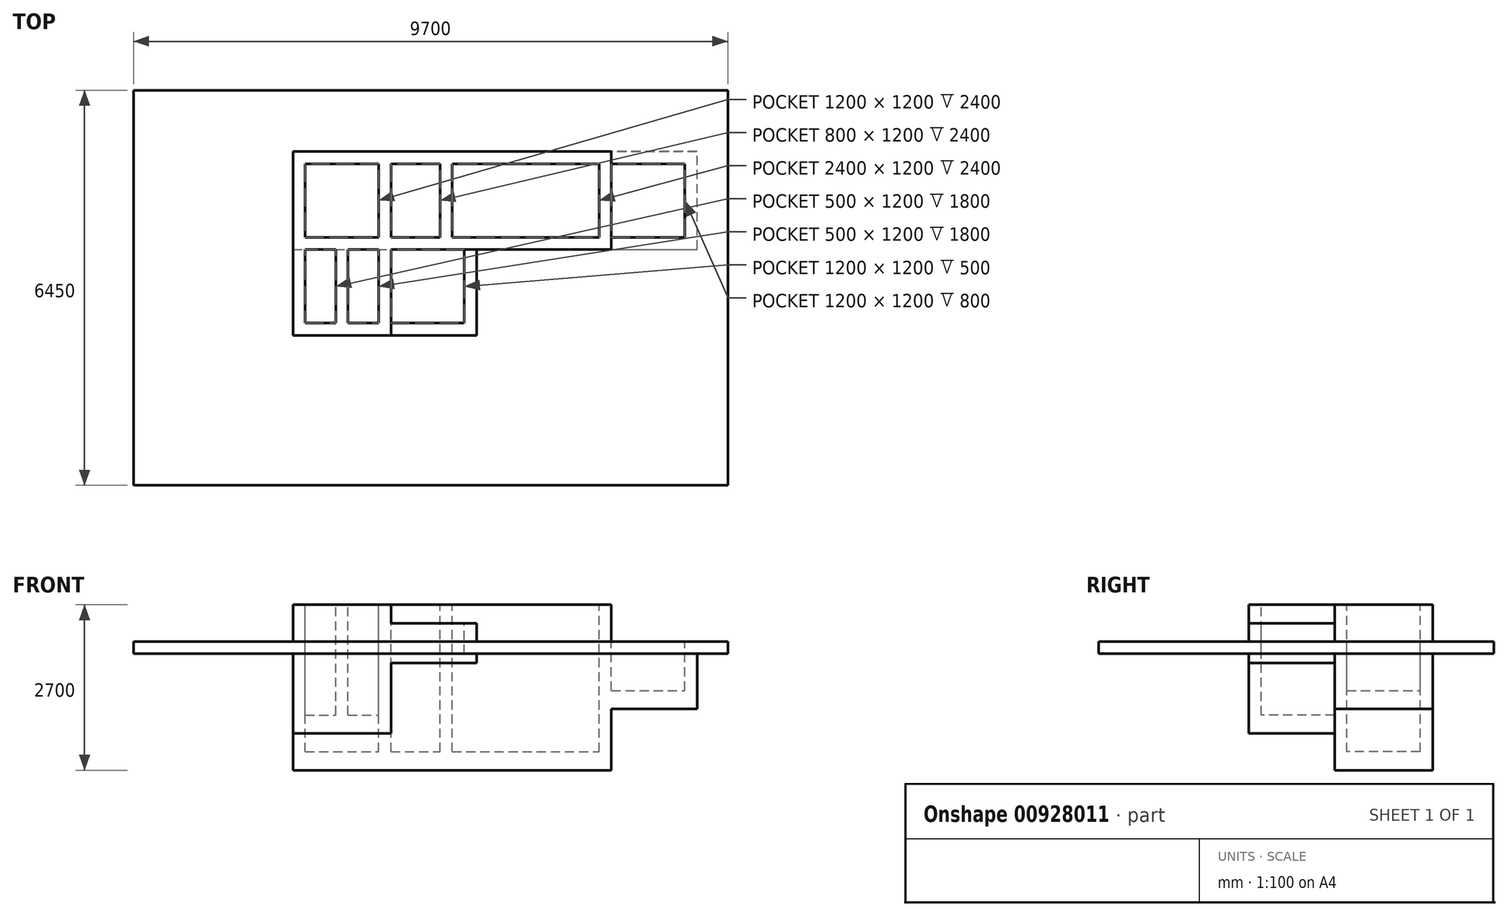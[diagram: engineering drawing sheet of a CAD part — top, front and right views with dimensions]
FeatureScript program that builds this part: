
annotation { "Feature Type Name" : "Feature", "Feature Type Description" : "" }
export const myFeature = defineFeature(function(context is Context, id is Id, definition is map)
    precondition{}
    {
        {
            var Q0;
            Q0=qCreatedBy(makeId("Top.planeOp"),FACE);
            var sketch = newSketch(context, id + "F0", { "sketchPlane" : qUnion([Q0])});
            skLineSegment(sketch, "E0.bottom", {"start": v(0, 0) * mm, "end": v(3000, 0) * mm});
            skLineSegment(sketch, "E0.top", {"start": v(0, 3000) * mm, "end": v(5200, 3000) * mm});
            skLineSegment(sketch, "E0.left", {"start": v(0, 0) * mm, "end": v(0, 3000) * mm});
            skLineSegment(sketch, "E0.right", {"start": v(5200, 1400) * mm, "end": v(5200, 3000) * mm});
            skLineSegment(sketch, "E1", {"start": v(5200, 1400) * mm, "end": v(3000, 1400) * mm});
            skLineSegment(sketch, "E2", {"start": v(3000, 1400) * mm, "end": v(3000, 0) * mm});
            skLineSegment(sketch, "E3.bottom", {"start": v(200, 2800) * mm, "end": v(1400, 2800) * mm});
            skLineSegment(sketch, "E3.top", {"start": v(200, 1600) * mm, "end": v(1400, 1600) * mm});
            skLineSegment(sketch, "E3.left", {"start": v(200, 2800) * mm, "end": v(200, 1600) * mm});
            skLineSegment(sketch, "E3.right", {"start": v(1400, 2800) * mm, "end": v(1400, 1600) * mm});
            skLineSegment(sketch, "E4.bottom", {"start": v(1600, 2800) * mm, "end": v(2400, 2800) * mm});
            skLineSegment(sketch, "E4.top", {"start": v(1600, 1600) * mm, "end": v(2400, 1600) * mm});
            skLineSegment(sketch, "E4.left", {"start": v(1600, 2800) * mm, "end": v(1600, 1600) * mm});
            skLineSegment(sketch, "E4.right", {"start": v(2400, 2800) * mm, "end": v(2400, 1600) * mm});
            skLineSegment(sketch, "E5.bottom", {"start": v(2600, 2800) * mm, "end": v(5000, 2800) * mm});
            skLineSegment(sketch, "E5.top", {"start": v(2600, 1600) * mm, "end": v(5000, 1600) * mm});
            skLineSegment(sketch, "E5.left", {"start": v(2600, 2800) * mm, "end": v(2600, 1600) * mm});
            skLineSegment(sketch, "E5.right", {"start": v(5000, 2800) * mm, "end": v(5000, 1600) * mm});
            skLineSegment(sketch, "E6", {"start": v(5200, 1400) * mm, "end": v(6600, 1400) * mm});
            skLineSegment(sketch, "E7", {"start": v(6600, 1400) * mm, "end": v(6600, 3000) * mm});
            skLineSegment(sketch, "E8", {"start": v(6600, 3000) * mm, "end": v(5200, 3000) * mm});
            skLineSegment(sketch, "E9.bottom", {"start": v(5200, 2800) * mm, "end": v(6400, 2800) * mm});
            skLineSegment(sketch, "E9.top", {"start": v(5200, 1600) * mm, "end": v(6400, 1600) * mm});
            skLineSegment(sketch, "E9.left", {"start": v(5200, 2800) * mm, "end": v(5200, 1600) * mm});
            skLineSegment(sketch, "E9.right", {"start": v(6400, 2800) * mm, "end": v(6400, 1600) * mm});
            skLineSegment(sketch, "E10.bottom", {"start": v(200, 1400) * mm, "end": v(700, 1400) * mm});
            skLineSegment(sketch, "E10.top", {"start": v(200, 200) * mm, "end": v(700, 200) * mm});
            skLineSegment(sketch, "E10.left", {"start": v(200, 1400) * mm, "end": v(200, 200) * mm});
            skLineSegment(sketch, "E10.right", {"start": v(700, 1400) * mm, "end": v(700, 200) * mm});
            skLineSegment(sketch, "E11.bottom", {"start": v(900, 1400) * mm, "end": v(1400, 1400) * mm});
            skLineSegment(sketch, "E11.top", {"start": v(900, 200) * mm, "end": v(1400, 200) * mm});
            skLineSegment(sketch, "E11.left", {"start": v(900, 1400) * mm, "end": v(900, 200) * mm});
            skLineSegment(sketch, "E11.right", {"start": v(1400, 1400) * mm, "end": v(1400, 200) * mm});
            skLineSegment(sketch, "E12.bottom", {"start": v(1600, 1400) * mm, "end": v(2800, 1400) * mm});
            skLineSegment(sketch, "E12.top", {"start": v(1600, 200) * mm, "end": v(2800, 200) * mm});
            skLineSegment(sketch, "E12.left", {"start": v(1600, 1400) * mm, "end": v(1600, 200) * mm});
            skLineSegment(sketch, "E12.right", {"start": v(2800, 1400) * mm, "end": v(2800, 200) * mm});
            skLineSegment(sketch, "E13", {"start": v(1400, 2800) * mm, "end": v(1400, 3000) * mm});
            skLineSegment(sketch, "E14", {"start": v(1400, 1600) * mm, "end": v(1400, 1400) * mm});
            skLineSegment(sketch, "E15", {"start": v(1600, 1400) * mm, "end": v(1600, 1600) * mm});
            skLineSegment(sketch, "E16", {"start": v(1400, 1600) * mm, "end": v(1600, 1600) * mm});
            skLineSegment(sketch, "E17", {"start": v(1600, 1400) * mm, "end": v(1400, 1400) * mm});
            skLineSegment(sketch, "E18", {"start": v(2600, 1600) * mm, "end": v(2600, 1400) * mm});
            skLineSegment(sketch, "E19", {"start": v(2400, 1600) * mm, "end": v(2400, 1400) * mm});
            skLineSegment(sketch, "E20", {"start": v(2600, 1600) * mm, "end": v(2400, 1600) * mm});
            skLineSegment(sketch, "E21", {"start": v(1600, 2800) * mm, "end": v(1600, 3000) * mm});
            skLineSegment(sketch, "E22", {"start": v(2400, 2800) * mm, "end": v(2400, 3000) * mm});
            skLineSegment(sketch, "E23", {"start": v(2600, 2800) * mm, "end": v(2600, 3000) * mm});
            skLineSegment(sketch, "E24", {"start": v(2400, 2800) * mm, "end": v(2600, 2800) * mm});
            skLineSegment(sketch, "E25", {"start": v(1600, 2800) * mm, "end": v(1400, 2800) * mm});
            skLineSegment(sketch, "E26", {"start": v(200, 2800) * mm, "end": v(200, 3000) * mm});
            skLineSegment(sketch, "E27", {"start": v(200, 2800) * mm, "end": v(0, 2800) * mm});
            skLineSegment(sketch, "E28", {"start": v(900, 1400) * mm, "end": v(900, 1600) * mm});
            skLineSegment(sketch, "E29", {"start": v(700, 1400) * mm, "end": v(700, 1600) * mm});
            skLineSegment(sketch, "E30", {"start": v(900, 1400) * mm, "end": v(700, 1400) * mm});
            skLineSegment(sketch, "E31", {"start": v(200, 1400) * mm, "end": v(200, 1600) * mm});
            skLineSegment(sketch, "E32", {"start": v(200, 1400) * mm, "end": v(0, 1400) * mm});
            skLineSegment(sketch, "E33", {"start": v(200, 1600) * mm, "end": v(0, 1600) * mm});
            skLineSegment(sketch, "E34", {"start": v(200, 200) * mm, "end": v(0, 200) * mm});
            skLineSegment(sketch, "E35", {"start": v(700, 200) * mm, "end": v(900, 200) * mm});
            skLineSegment(sketch, "E36", {"start": v(1400, 200) * mm, "end": v(1600, 200) * mm});
            skLineSegment(sketch, "E37", {"start": v(2800, 200) * mm, "end": v(3000, 200) * mm});
            skLineSegment(sketch, "E38", {"start": v(2800, 200) * mm, "end": v(2800, 0) * mm});
            skLineSegment(sketch, "E39", {"start": v(1600, 200) * mm, "end": v(1600, 0) * mm});
            skLineSegment(sketch, "E40", {"start": v(1400, 200) * mm, "end": v(1400, 0) * mm});
            skLineSegment(sketch, "E41", {"start": v(700, 200) * mm, "end": v(700, 0) * mm});
            skLineSegment(sketch, "E42", {"start": v(900, 200) * mm, "end": v(900, 0) * mm});
            skLineSegment(sketch, "E43", {"start": v(200, 200) * mm, "end": v(200, 0) * mm});
            skLineSegment(sketch, "E44", {"start": v(2800, 1400) * mm, "end": v(3000, 1400) * mm});
            skLineSegment(sketch, "E45", {"start": v(5000, 1600) * mm, "end": v(5200, 1600) * mm});
            skLineSegment(sketch, "E46", {"start": v(5200, 2800) * mm, "end": v(5000, 2800) * mm});
            skLineSegment(sketch, "E47", {"start": v(5000, 2800) * mm, "end": v(5000, 3000) * mm});
            skLineSegment(sketch, "E48", {"start": v(5200, 2800) * mm, "end": v(5200, 3000) * mm});
            skLineSegment(sketch, "E49", {"start": v(6400, 2800) * mm, "end": v(6400, 3000) * mm});
            skLineSegment(sketch, "E50", {"start": v(6400, 2800) * mm, "end": v(6600, 2800) * mm});
            skLineSegment(sketch, "E51", {"start": v(6400, 1600) * mm, "end": v(6600, 1600) * mm});
            skLineSegment(sketch, "E52", {"start": v(6400, 1600) * mm, "end": v(6400, 1400) * mm});
            skLineSegment(sketch, "E53", {"start": v(5200, 1600) * mm, "end": v(5200, 1400) * mm});
            skLineSegment(sketch, "E54", {"start": v(5000, 1600) * mm, "end": v(5000, 1400) * mm});
            skPoint(sketch, "E55.orphan", {"position": v(5200, 3000) * mm});
            skSolve(sketch);
        }
        {
            var Q0;
            {var subQ3=sQuery(id+"F0.wireOp",EDGE,"E26");Q0=makeQuery(id+"F0.imprint","IMPRINT",FACE,{"disambiguationData":[TD([[makeQuery(id+"F0.imprint","IMPRINT",EDGE,{"derivedFrom":subQ3}),1.0]])]});}
            var Q1;
            Q1=makeQuery(id+"F0.imprint","IMPRINT",FACE,{"disambiguationData":[TD([[makeQuery(id+"F0.imprint","IMPRINT",EDGE,{"derivedFrom":sQuery(id+"F0.wireOp",EDGE,"E3.left")}),-1.0]])]});
            var Q2;
            Q2=makeQuery(id+"F0.imprint","IMPRINT",FACE,{"disambiguationData":[TD([[makeQuery(id+"F0.imprint","IMPRINT",EDGE,{"derivedFrom":sQuery(id+"F0.wireOp",EDGE,"E31")}),1.0]])]});
            var Q3;
            Q3=makeQuery(id+"F0.imprint","IMPRINT",FACE,{"disambiguationData":[TD([[makeQuery(id+"F0.imprint","IMPRINT",EDGE,{"derivedFrom":sQuery(id+"F0.wireOp",EDGE,"E10.bottom")}),1.0]])]});
            var Q4;
            {var subQ0=sQuery(id+"F0.wireOp",EDGE,"E28");Q4=makeQuery(id+"F0.imprint","IMPRINT",FACE,{"disambiguationData":[TD([[makeQuery(id+"F0.imprint","IMPRINT",EDGE,{"derivedFrom":subQ0}),1.0]])]});}
            var Q5;
            Q5=makeQuery(id+"F0.imprint","IMPRINT",FACE,{"disambiguationData":[TD([[makeQuery(id+"F0.imprint","IMPRINT",EDGE,{"derivedFrom":sQuery(id+"F0.wireOp",EDGE,"E11.bottom")}),1.0]])]});
            var Q6;
            Q6=makeQuery(id+"F0.imprint","IMPRINT",FACE,{"disambiguationData":[TD([[makeQuery(id+"F0.imprint","IMPRINT",EDGE,{"derivedFrom":sQuery(id+"F0.wireOp",EDGE,"E14")}),1.0]])]});
            var Q7;
            Q7=makeQuery(id+"F0.imprint","IMPRINT",FACE,{"disambiguationData":[TD([[makeQuery(id+"F0.imprint","IMPRINT",EDGE,{"derivedFrom":sQuery(id+"F0.wireOp",EDGE,"E3.right")}),1.0]])]});
            var Q8;
            {var subQ0=sQuery(id+"F0.wireOp",EDGE,"E13");Q8=makeQuery(id+"F0.imprint","IMPRINT",FACE,{"disambiguationData":[TD([[makeQuery(id+"F0.imprint","IMPRINT",EDGE,{"derivedFrom":subQ0}),-1.0]])]});}
            var Q9;
            Q9=makeQuery(id+"F0.imprint","IMPRINT",FACE,{"disambiguationData":[TD([[makeQuery(id+"F0.imprint","IMPRINT",EDGE,{"derivedFrom":sQuery(id+"F0.wireOp",EDGE,"E3.bottom")}),1.0]])]});
            extrude(context, id + "F1", {"entities" : qUnion([Q0, Q1, Q2, Q3, Q4, Q5, Q6, Q7, Q8, Q9]), "oppositeDirection" : true, "depth" : 1800 * mm, "offsetDistance" : 25 * mm});
        }
        {
            var Q0;
            Q0=makeQuery(id+"F0.imprint","IMPRINT",FACE,{"disambiguationData":[TD([[makeQuery(id+"F0.imprint","IMPRINT",EDGE,{"derivedFrom":sQuery(id+"F0.wireOp",EDGE,"E31")}),1.0]])]});
            var Q1;
            Q1=makeQuery(id+"F0.imprint","IMPRINT",FACE,{"disambiguationData":[TD([[makeQuery(id+"F0.imprint","IMPRINT",EDGE,{"derivedFrom":sQuery(id+"F0.wireOp",EDGE,"E10.bottom")}),1.0]])]});
            var Q2;
            {var subQ0=sQuery(id+"F0.wireOp",EDGE,"E28");Q2=makeQuery(id+"F0.imprint","IMPRINT",FACE,{"disambiguationData":[TD([[makeQuery(id+"F0.imprint","IMPRINT",EDGE,{"derivedFrom":subQ0}),1.0]])]});}
            var Q3;
            Q3=makeQuery(id+"F0.imprint","IMPRINT",FACE,{"disambiguationData":[TD([[makeQuery(id+"F0.imprint","IMPRINT",EDGE,{"derivedFrom":sQuery(id+"F0.wireOp",EDGE,"E11.bottom")}),1.0]])]});
            var Q4;
            Q4=makeQuery(id+"F0.imprint","IMPRINT",FACE,{"disambiguationData":[TD([[makeQuery(id+"F0.imprint","IMPRINT",EDGE,{"derivedFrom":sQuery(id+"F0.wireOp",EDGE,"E14")}),1.0]])]});
            var Q5;
            Q5=makeQuery(id+"F0.imprint","IMPRINT",FACE,{"disambiguationData":[TD([[makeQuery(id+"F0.imprint","IMPRINT",EDGE,{"derivedFrom":sQuery(id+"F0.wireOp",EDGE,"E3.right")}),1.0]])]});
            var Q6;
            {var subQ0=sQuery(id+"F0.wireOp",EDGE,"E13");Q6=makeQuery(id+"F0.imprint","IMPRINT",FACE,{"disambiguationData":[TD([[makeQuery(id+"F0.imprint","IMPRINT",EDGE,{"derivedFrom":subQ0}),-1.0]])]});}
            var Q7;
            Q7=makeQuery(id+"F0.imprint","IMPRINT",FACE,{"disambiguationData":[TD([[makeQuery(id+"F0.imprint","IMPRINT",EDGE,{"derivedFrom":sQuery(id+"F0.wireOp",EDGE,"E3.bottom")}),1.0]])]});
            var Q8;
            {var subQ3=sQuery(id+"F0.wireOp",EDGE,"E26");Q8=makeQuery(id+"F0.imprint","IMPRINT",FACE,{"disambiguationData":[TD([[makeQuery(id+"F0.imprint","IMPRINT",EDGE,{"derivedFrom":subQ3}),1.0]])]});}
            var Q9;
            Q9=makeQuery(id+"F0.imprint","IMPRINT",FACE,{"disambiguationData":[TD([[makeQuery(id+"F0.imprint","IMPRINT",EDGE,{"derivedFrom":sQuery(id+"F0.wireOp",EDGE,"E3.left")}),-1.0]])]});
            extrude(context, id + "F2", {"entities" : qUnion([Q0, Q1, Q2, Q3, Q4, Q5, Q6, Q7, Q8, Q9]), "operationType" : NewBodyOperationType.ADD, "depth" : 600 * mm, "offsetDistance" : 25 * mm});
        }
        {
            var Q0;
            Q0=makeQuery(id+"F1.opExtrude","CAP_FACE",FACE,{"disambiguationData":[OSD([sQuery(id+"F0.wireOp",EDGE,"E0.top"),sQuery(id+"F0.wireOp",EDGE,"E0.left"),sQuery(id+"F0.wireOp",EDGE,"E3.bottom"),sQuery(id+"F0.wireOp",EDGE,"E3.top"),sQuery(id+"F0.wireOp",EDGE,"E3.left"),sQuery(id+"F0.wireOp",EDGE,"E3.right"),sQuery(id+"F0.wireOp",EDGE,"E4.left"),sQuery(id+"F0.wireOp",EDGE,"E10.bottom"),sQuery(id+"F0.wireOp",EDGE,"E11.bottom"),sQuery(id+"F0.wireOp",EDGE,"E15"),sQuery(id+"F0.wireOp",EDGE,"E17"),sQuery(id+"F0.wireOp",EDGE,"E21"),sQuery(id+"F0.wireOp",EDGE,"E30"),sQuery(id+"F0.wireOp",EDGE,"E32")])],"isStart":false});
            var sketch = newSketch(context, id + "F3", { "sketchPlane" : qUnion([Q0])});
            skLineSegment(sketch, "E56.0", {"start": v(200, -1400) * mm, "end": v(0, -1400) * mm});
            skLineSegment(sketch, "E57", {"start": v(0, -1400) * mm, "end": v(0, -3000) * mm});
            skLineSegment(sketch, "E58", {"start": v(0, -3000) * mm, "end": v(1600, -3000) * mm});
            skLineSegment(sketch, "E59", {"start": v(1600, -3000) * mm, "end": v(1600, -1400) * mm});
            skLineSegment(sketch, "E60", {"start": v(1600, -1400) * mm, "end": v(200, -1400) * mm});
            skLineSegment(sketch, "E61.bottom", {"start": v(1400, -1400) * mm, "end": v(2600, -1400) * mm});
            skLineSegment(sketch, "E61.top", {"start": v(1400, -3000) * mm, "end": v(2600, -3000) * mm});
            skLineSegment(sketch, "E61.left", {"start": v(1400, -1400) * mm, "end": v(1400, -3000) * mm});
            skLineSegment(sketch, "E62.0", {"start": v(2600, -1600) * mm, "end": v(2600, -1400) * mm});
            skLineSegment(sketch, "E62.1", {"start": v(2600, -2800) * mm, "end": v(2600, -1600) * mm});
            skLineSegment(sketch, "E62.2", {"start": v(2600, -2800) * mm, "end": v(2600, -3000) * mm});
            skLineSegment(sketch, "E63.bottom", {"start": v(2600, -1400) * mm, "end": v(5200, -1400) * mm});
            skLineSegment(sketch, "E63.top", {"start": v(2600, -3000) * mm, "end": v(5200, -3000) * mm});
            skLineSegment(sketch, "E63.left", {"start": v(2600, -1400) * mm, "end": v(2600, -3000) * mm});
            skLineSegment(sketch, "E64.0", {"start": v(5200, -1400) * mm, "end": v(5200, -3000) * mm});
            skLineSegment(sketch, "E65.bottom", {"start": v(0, -1400) * mm, "end": v(1600, -1400) * mm});
            skLineSegment(sketch, "E65.top", {"start": v(0, 0) * mm, "end": v(1600, 0) * mm});
            skLineSegment(sketch, "E65.left", {"start": v(0, -1400) * mm, "end": v(0, 0) * mm});
            skLineSegment(sketch, "E66.0", {"start": v(1600, -1400) * mm, "end": v(1600, -200) * mm});
            skLineSegment(sketch, "E67", {"start": v(1600, -200) * mm, "end": v(1600, 0) * mm});
            skSolve(sketch);
        }
        {
            var Q0;
            Q0=makeQuery(id+"F3.imprint","IMPRINT",FACE,{"disambiguationData":[TD([[makeQuery(id+"F3.imprint","IMPRINT",EDGE,{"derivedFrom":sQuery(id+"F3.wireOp",EDGE,"E56.0")}),1.0]])]});
            var Q1;
            {var subQ1=makeQuery(id+"F1.opExtrude","CAP_EDGE",EDGE,{"disambiguationData":[OSD([sQuery(id+"F0.wireOp",EDGE,"E3.bottom")])],"isStart":false});Q1=makeQuery(id+"F3.imprint","IMPRINT",FACE,{"disambiguationData":[TD([[makeQuery(id+"F3.imprint","IMPRINT",EDGE,{"derivedFrom":subQ1}),1.0]])]});}
            var Q2;
            {var subQ4=sQuery(id+"F3.wireOp",EDGE,"E59");Q2=makeQuery(id+"F3.imprint","IMPRINT",FACE,{"disambiguationData":[TD([[makeQuery(id+"F3.imprint","IMPRINT",EDGE,{"derivedFrom":subQ4}),-1.0]])]});}
            var Q3;
            {var subQ6=sQuery(id+"F3.wireOp",EDGE,"E57");Q3=makeQuery(id+"F3.imprint","IMPRINT",FACE,{"disambiguationData":[TD([[makeQuery(id+"F3.imprint","IMPRINT",EDGE,{"derivedFrom":subQ6}),1.0]])]});}
            extrude(context, id + "F4", {"entities" : qUnion([Q0, Q1, Q2, Q3]), "operationType" : NewBodyOperationType.ADD, "depth" : 300 * mm, "offsetDistance" : 25 * mm});
        }
        {
            var Q0;
            Q0=makeQuery(id+"F0.imprint","IMPRINT",FACE,{"disambiguationData":[TD([[makeQuery(id+"F0.imprint","IMPRINT",EDGE,{"derivedFrom":sQuery(id+"F0.wireOp",EDGE,"E4.top")}),-1.0]])]});
            var Q1;
            {var subQ0=sQuery(id+"F0.wireOp",EDGE,"E18");Q1=makeQuery(id+"F0.imprint","IMPRINT",FACE,{"disambiguationData":[TD([[makeQuery(id+"F0.imprint","IMPRINT",EDGE,{"derivedFrom":subQ0}),-1.0]])]});}
            var Q2;
            Q2=makeQuery(id+"F0.imprint","IMPRINT",FACE,{"disambiguationData":[TD([[makeQuery(id+"F0.imprint","IMPRINT",EDGE,{"derivedFrom":sQuery(id+"F0.wireOp",EDGE,"E4.right")}),1.0]])]});
            var Q3;
            {var subQ0=sQuery(id+"F0.wireOp",EDGE,"E22");Q3=makeQuery(id+"F0.imprint","IMPRINT",FACE,{"disambiguationData":[TD([[makeQuery(id+"F0.imprint","IMPRINT",EDGE,{"derivedFrom":subQ0}),-1.0]])]});}
            var Q4;
            Q4=makeQuery(id+"F0.imprint","IMPRINT",FACE,{"disambiguationData":[TD([[makeQuery(id+"F0.imprint","IMPRINT",EDGE,{"derivedFrom":sQuery(id+"F0.wireOp",EDGE,"E4.bottom")}),1.0]])]});
            extrude(context, id + "F5", {"entities" : qUnion([Q0, Q1, Q2, Q3, Q4]), "operationType" : NewBodyOperationType.ADD, "oppositeDirection" : true, "depth" : 1800 * mm, "offsetDistance" : 25 * mm});
        }
        {
            var Q0;
            Q0=makeQuery(id+"F0.imprint","IMPRINT",FACE,{"disambiguationData":[TD([[makeQuery(id+"F0.imprint","IMPRINT",EDGE,{"derivedFrom":sQuery(id+"F0.wireOp",EDGE,"E4.bottom")}),1.0]])]});
            var Q1;
            {var subQ0=sQuery(id+"F0.wireOp",EDGE,"E22");Q1=makeQuery(id+"F0.imprint","IMPRINT",FACE,{"disambiguationData":[TD([[makeQuery(id+"F0.imprint","IMPRINT",EDGE,{"derivedFrom":subQ0}),-1.0]])]});}
            var Q2;
            Q2=makeQuery(id+"F0.imprint","IMPRINT",FACE,{"disambiguationData":[TD([[makeQuery(id+"F0.imprint","IMPRINT",EDGE,{"derivedFrom":sQuery(id+"F0.wireOp",EDGE,"E4.right")}),1.0]])]});
            var Q3;
            {var subQ0=sQuery(id+"F0.wireOp",EDGE,"E18");Q3=makeQuery(id+"F0.imprint","IMPRINT",FACE,{"disambiguationData":[TD([[makeQuery(id+"F0.imprint","IMPRINT",EDGE,{"derivedFrom":subQ0}),-1.0]])]});}
            var Q4;
            Q4=makeQuery(id+"F0.imprint","IMPRINT",FACE,{"disambiguationData":[TD([[makeQuery(id+"F0.imprint","IMPRINT",EDGE,{"derivedFrom":sQuery(id+"F0.wireOp",EDGE,"E4.top")}),-1.0]])]});
            extrude(context, id + "F6", {"entities" : qUnion([Q0, Q1, Q2, Q3, Q4]), "operationType" : NewBodyOperationType.ADD, "depth" : 600 * mm, "offsetDistance" : 25 * mm});
        }
        {
            var Q0;
            {var subQ2=sQuery(id+"F3.wireOp",EDGE,"E59");Q0=makeQuery(id+"F3.imprint","IMPRINT",FACE,{"disambiguationData":[TD([[makeQuery(id+"F3.imprint","IMPRINT",EDGE,{"derivedFrom":subQ2}),1.0]])]});}
            extrude(context, id + "F7", {"entities" : qUnion([Q0]), "operationType" : NewBodyOperationType.ADD, "depth" : 300 * mm, "offsetDistance" : 25 * mm});
        }
        {
            var Q0;
            Q0=makeQuery(id+"F0.imprint","IMPRINT",FACE,{"disambiguationData":[TD([[makeQuery(id+"F0.imprint","IMPRINT",EDGE,{"derivedFrom":sQuery(id+"F0.wireOp",EDGE,"E5.bottom")}),1.0]])]});
            var Q1;
            {var subQ3=sQuery(id+"F0.wireOp",EDGE,"E47");Q1=makeQuery(id+"F0.imprint","IMPRINT",FACE,{"disambiguationData":[TD([[makeQuery(id+"F0.imprint","IMPRINT",EDGE,{"derivedFrom":subQ3}),-1.0]])]});}
            var Q2;
            {var subQ5=sQuery(id+"F0.wireOp",EDGE,"E5.right");Q2=makeQuery(id+"F0.imprint","IMPRINT",FACE,{"disambiguationData":[TD([[makeQuery(id+"F0.imprint","IMPRINT",EDGE,{"derivedFrom":subQ5}),1.0]])]});}
            var Q3;
            {var subQ5=sQuery(id+"F0.wireOp",EDGE,"E54");Q3=makeQuery(id+"F0.imprint","IMPRINT",FACE,{"disambiguationData":[TD([[makeQuery(id+"F0.imprint","IMPRINT",EDGE,{"derivedFrom":subQ5}),1.0]])]});}
            var Q4;
            Q4=makeQuery(id+"F0.imprint","IMPRINT",FACE,{"disambiguationData":[TD([[makeQuery(id+"F0.imprint","IMPRINT",EDGE,{"derivedFrom":sQuery(id+"F0.wireOp",EDGE,"E5.top")}),-1.0]])]});
            extrude(context, id + "F8", {"entities" : qUnion([Q0, Q1, Q2, Q3, Q4]), "operationType" : NewBodyOperationType.ADD, "oppositeDirection" : true, "depth" : 1800 * mm, "offsetDistance" : 25 * mm});
        }
        {
            var Q0;
            Q0=makeQuery(id+"F0.imprint","IMPRINT",FACE,{"disambiguationData":[TD([[makeQuery(id+"F0.imprint","IMPRINT",EDGE,{"derivedFrom":sQuery(id+"F0.wireOp",EDGE,"E5.top")}),-1.0]])]});
            var Q1;
            {var subQ5=sQuery(id+"F0.wireOp",EDGE,"E54");Q1=makeQuery(id+"F0.imprint","IMPRINT",FACE,{"disambiguationData":[TD([[makeQuery(id+"F0.imprint","IMPRINT",EDGE,{"derivedFrom":subQ5}),1.0]])]});}
            var Q2;
            {var subQ5=sQuery(id+"F0.wireOp",EDGE,"E5.right");Q2=makeQuery(id+"F0.imprint","IMPRINT",FACE,{"disambiguationData":[TD([[makeQuery(id+"F0.imprint","IMPRINT",EDGE,{"derivedFrom":subQ5}),1.0]])]});}
            var Q3;
            {var subQ3=sQuery(id+"F0.wireOp",EDGE,"E47");Q3=makeQuery(id+"F0.imprint","IMPRINT",FACE,{"disambiguationData":[TD([[makeQuery(id+"F0.imprint","IMPRINT",EDGE,{"derivedFrom":subQ3}),-1.0]])]});}
            var Q4;
            Q4=makeQuery(id+"F0.imprint","IMPRINT",FACE,{"disambiguationData":[TD([[makeQuery(id+"F0.imprint","IMPRINT",EDGE,{"derivedFrom":sQuery(id+"F0.wireOp",EDGE,"E5.bottom")}),1.0]])]});
            extrude(context, id + "F9", {"entities" : qUnion([Q0, Q1, Q2, Q3, Q4]), "operationType" : NewBodyOperationType.ADD, "depth" : 600 * mm, "offsetDistance" : 25 * mm});
        }
        {
            var Q0;
            Q0=makeQuery(id+"F3.imprint","IMPRINT",FACE,{"disambiguationData":[TD([[makeQuery(id+"F3.imprint","IMPRINT",EDGE,{"derivedFrom":sQuery(id+"F3.wireOp",EDGE,"E63.bottom")}),-1.0]])]});
            extrude(context, id + "F10", {"entities" : qUnion([Q0]), "operationType" : NewBodyOperationType.ADD, "depth" : 300 * mm, "offsetDistance" : 25 * mm});
        }
        {
            var Q0;
            Q0=makeQuery(id+"F0.imprint","IMPRINT",FACE,{"disambiguationData":[TD([[makeQuery(id+"F0.imprint","IMPRINT",EDGE,{"derivedFrom":sQuery(id+"F0.wireOp",EDGE,"E10.left")}),-1.0]])]});
            var Q1;
            {var subQ4=sQuery(id+"F0.wireOp",EDGE,"E34");Q1=makeQuery(id+"F0.imprint","IMPRINT",FACE,{"disambiguationData":[TD([[makeQuery(id+"F0.imprint","IMPRINT",EDGE,{"derivedFrom":subQ4}),1.0]])]});}
            var Q2;
            Q2=makeQuery(id+"F0.imprint","IMPRINT",FACE,{"disambiguationData":[TD([[makeQuery(id+"F0.imprint","IMPRINT",EDGE,{"derivedFrom":sQuery(id+"F0.wireOp",EDGE,"E10.top")}),-1.0]])]});
            var Q3;
            Q3=makeQuery(id+"F0.imprint","IMPRINT",FACE,{"disambiguationData":[TD([[makeQuery(id+"F0.imprint","IMPRINT",EDGE,{"derivedFrom":sQuery(id+"F0.wireOp",EDGE,"E35")}),-1.0]])]});
            var Q4;
            Q4=makeQuery(id+"F0.imprint","IMPRINT",FACE,{"disambiguationData":[TD([[makeQuery(id+"F0.imprint","IMPRINT",EDGE,{"derivedFrom":sQuery(id+"F0.wireOp",EDGE,"E10.right")}),1.0]])]});
            var Q5;
            Q5=makeQuery(id+"F0.imprint","IMPRINT",FACE,{"disambiguationData":[TD([[makeQuery(id+"F0.imprint","IMPRINT",EDGE,{"derivedFrom":sQuery(id+"F0.wireOp",EDGE,"E11.top")}),-1.0]])]});
            var Q6;
            Q6=makeQuery(id+"F0.imprint","IMPRINT",FACE,{"disambiguationData":[TD([[makeQuery(id+"F0.imprint","IMPRINT",EDGE,{"derivedFrom":sQuery(id+"F0.wireOp",EDGE,"E36")}),-1.0]])]});
            var Q7;
            Q7=makeQuery(id+"F0.imprint","IMPRINT",FACE,{"disambiguationData":[TD([[makeQuery(id+"F0.imprint","IMPRINT",EDGE,{"derivedFrom":sQuery(id+"F0.wireOp",EDGE,"E11.right")}),1.0]])]});
            extrude(context, id + "F11", {"entities" : qUnion([Q0, Q1, Q2, Q3, Q4, Q5, Q6, Q7]), "operationType" : NewBodyOperationType.ADD, "oppositeDirection" : true, "depth" : 1200 * mm, "offsetDistance" : 25 * mm});
        }
        {
            var Q0;
            Q0=makeQuery(id+"F0.imprint","IMPRINT",FACE,{"disambiguationData":[TD([[makeQuery(id+"F0.imprint","IMPRINT",EDGE,{"derivedFrom":sQuery(id+"F0.wireOp",EDGE,"E11.right")}),1.0]])]});
            var Q1;
            Q1=makeQuery(id+"F0.imprint","IMPRINT",FACE,{"disambiguationData":[TD([[makeQuery(id+"F0.imprint","IMPRINT",EDGE,{"derivedFrom":sQuery(id+"F0.wireOp",EDGE,"E36")}),-1.0]])]});
            var Q2;
            Q2=makeQuery(id+"F0.imprint","IMPRINT",FACE,{"disambiguationData":[TD([[makeQuery(id+"F0.imprint","IMPRINT",EDGE,{"derivedFrom":sQuery(id+"F0.wireOp",EDGE,"E11.top")}),-1.0]])]});
            var Q3;
            Q3=makeQuery(id+"F0.imprint","IMPRINT",FACE,{"disambiguationData":[TD([[makeQuery(id+"F0.imprint","IMPRINT",EDGE,{"derivedFrom":sQuery(id+"F0.wireOp",EDGE,"E35")}),-1.0]])]});
            var Q4;
            Q4=makeQuery(id+"F0.imprint","IMPRINT",FACE,{"disambiguationData":[TD([[makeQuery(id+"F0.imprint","IMPRINT",EDGE,{"derivedFrom":sQuery(id+"F0.wireOp",EDGE,"E10.right")}),1.0]])]});
            var Q5;
            Q5=makeQuery(id+"F0.imprint","IMPRINT",FACE,{"disambiguationData":[TD([[makeQuery(id+"F0.imprint","IMPRINT",EDGE,{"derivedFrom":sQuery(id+"F0.wireOp",EDGE,"E10.top")}),-1.0]])]});
            var Q6;
            {var subQ4=sQuery(id+"F0.wireOp",EDGE,"E34");Q6=makeQuery(id+"F0.imprint","IMPRINT",FACE,{"disambiguationData":[TD([[makeQuery(id+"F0.imprint","IMPRINT",EDGE,{"derivedFrom":subQ4}),1.0]])]});}
            var Q7;
            Q7=makeQuery(id+"F0.imprint","IMPRINT",FACE,{"disambiguationData":[TD([[makeQuery(id+"F0.imprint","IMPRINT",EDGE,{"derivedFrom":sQuery(id+"F0.wireOp",EDGE,"E10.left")}),-1.0]])]});
            extrude(context, id + "F12", {"entities" : qUnion([Q0, Q1, Q2, Q3, Q4, Q5, Q6, Q7]), "operationType" : NewBodyOperationType.ADD, "depth" : 600 * mm, "offsetDistance" : 25 * mm});
        }
        {
            var Q0;
            Q0=makeQuery(id+"F11.opExtrude","CAP_FACE",FACE,{"disambiguationData":[OSD([sQuery(id+"F0.wireOp",EDGE,"E0.bottom"),sQuery(id+"F0.wireOp",EDGE,"E0.left"),sQuery(id+"F0.wireOp",EDGE,"E10.top"),sQuery(id+"F0.wireOp",EDGE,"E10.left"),sQuery(id+"F0.wireOp",EDGE,"E10.right"),sQuery(id+"F0.wireOp",EDGE,"E11.top"),sQuery(id+"F0.wireOp",EDGE,"E11.left"),sQuery(id+"F0.wireOp",EDGE,"E11.right"),sQuery(id+"F0.wireOp",EDGE,"E12.left"),sQuery(id+"F0.wireOp",EDGE,"E17"),sQuery(id+"F0.wireOp",EDGE,"E30"),sQuery(id+"F0.wireOp",EDGE,"E32"),sQuery(id+"F0.wireOp",EDGE,"E39")])],"isStart":false});
            var sketch = newSketch(context, id + "F13", { "sketchPlane" : qUnion([Q0])});
            skLineSegment(sketch, "E68.0", {"start": v(0, 0) * mm, "end": v(1600, 0) * mm});
            skLineSegment(sketch, "E68.1", {"start": v(0, -1400) * mm, "end": v(0, 0) * mm});
            skLineSegment(sketch, "E68.2", {"start": v(0, -1400) * mm, "end": v(1600, -1400) * mm});
            skLineSegment(sketch, "E68.3", {"start": v(1600, -1400) * mm, "end": v(1600, -200) * mm});
            skLineSegment(sketch, "E69", {"start": v(1600, 0) * mm, "end": v(1600, -200) * mm});
            skSolve(sketch);
        }
        {
            var Q0;
            Q0 = qSketchRegion(id + "F13", true);
            extrude(context, id + "F14", {"entities" : qUnion([Q0]), "operationType" : NewBodyOperationType.ADD, "depth" : 300 * mm, "offsetDistance" : 25 * mm});
        }
        {
            var Q0;
            Q0=makeQuery(id+"F0.imprint","IMPRINT",FACE,{"disambiguationData":[TD([[makeQuery(id+"F0.imprint","IMPRINT",EDGE,{"derivedFrom":sQuery(id+"F0.wireOp",EDGE,"E12.right")}),1.0]])]});
            var Q1;
            {var subQ4=sQuery(id+"F0.wireOp",EDGE,"E37");Q1=makeQuery(id+"F0.imprint","IMPRINT",FACE,{"disambiguationData":[TD([[makeQuery(id+"F0.imprint","IMPRINT",EDGE,{"derivedFrom":subQ4}),-1.0]])]});}
            var Q2;
            Q2=makeQuery(id+"F0.imprint","IMPRINT",FACE,{"disambiguationData":[TD([[makeQuery(id+"F0.imprint","IMPRINT",EDGE,{"derivedFrom":sQuery(id+"F0.wireOp",EDGE,"E12.top")}),-1.0]])]});
            extrude(context, id + "F15", {"entities" : qUnion([Q0, Q1, Q2]), "oppositeDirection" : true, "depth" : 200 * mm, "offsetDistance" : 25 * mm});
        }
        {
            var Q0;
            Q0=makeQuery(id+"F0.imprint","IMPRINT",FACE,{"disambiguationData":[TD([[makeQuery(id+"F0.imprint","IMPRINT",EDGE,{"derivedFrom":sQuery(id+"F0.wireOp",EDGE,"E12.right")}),1.0]])]});
            var Q1;
            {var subQ4=sQuery(id+"F0.wireOp",EDGE,"E37");Q1=makeQuery(id+"F0.imprint","IMPRINT",FACE,{"disambiguationData":[TD([[makeQuery(id+"F0.imprint","IMPRINT",EDGE,{"derivedFrom":subQ4}),-1.0]])]});}
            var Q2;
            Q2=makeQuery(id+"F0.imprint","IMPRINT",FACE,{"disambiguationData":[TD([[makeQuery(id+"F0.imprint","IMPRINT",EDGE,{"derivedFrom":sQuery(id+"F0.wireOp",EDGE,"E12.top")}),-1.0]])]});
            extrude(context, id + "F16", {"entities" : qUnion([Q0, Q1, Q2]), "operationType" : NewBodyOperationType.ADD, "depth" : 300 * mm, "offsetDistance" : 25 * mm});
        }
        {
            var Q0;
            Q0=makeQuery(id+"F15.opExtrude","CAP_FACE",FACE,{"disambiguationData":[OSD([sQuery(id+"F0.wireOp",EDGE,"E0.bottom"),sQuery(id+"F0.wireOp",EDGE,"E2"),sQuery(id+"F0.wireOp",EDGE,"E12.top"),sQuery(id+"F0.wireOp",EDGE,"E12.right"),sQuery(id+"F0.wireOp",EDGE,"E39"),sQuery(id+"F0.wireOp",EDGE,"E44")])],"isStart":false});
            var sketch = newSketch(context, id + "F17", { "sketchPlane" : qUnion([Q0])});
            skLineSegment(sketch, "E70.bottom", {"start": v(3000, 0) * mm, "end": v(1600, 0) * mm});
            skLineSegment(sketch, "E70.top", {"start": v(3000, -1400) * mm, "end": v(1600, -1400) * mm});
            skLineSegment(sketch, "E70.left", {"start": v(3000, 0) * mm, "end": v(3000, -1400) * mm});
            skLineSegment(sketch, "E70.right", {"start": v(1600, 0) * mm, "end": v(1600, -1400) * mm});
            skSolve(sketch);
        }
        {
            var Q0;
            Q0 = qSketchRegion(id + "F17", true);
            extrude(context, id + "F18", {"entities" : qUnion([Q0]), "operationType" : NewBodyOperationType.ADD, "depth" : 150 * mm, "offsetDistance" : 25 * mm});
        }
        {
            var Q0;
            Q0=makeQuery(id+"F0.imprint","IMPRINT",FACE,{"disambiguationData":[TD([[makeQuery(id+"F0.imprint","IMPRINT",EDGE,{"derivedFrom":sQuery(id+"F0.wireOp",EDGE,"E9.bottom")}),1.0]])]});
            var Q1;
            {var subQ4=sQuery(id+"F0.wireOp",EDGE,"E49");Q1=makeQuery(id+"F0.imprint","IMPRINT",FACE,{"disambiguationData":[TD([[makeQuery(id+"F0.imprint","IMPRINT",EDGE,{"derivedFrom":subQ4}),-1.0]])]});}
            var Q2;
            Q2=makeQuery(id+"F0.imprint","IMPRINT",FACE,{"disambiguationData":[TD([[makeQuery(id+"F0.imprint","IMPRINT",EDGE,{"derivedFrom":sQuery(id+"F0.wireOp",EDGE,"E9.right")}),1.0]])]});
            var Q3;
            {var subQ4=sQuery(id+"F0.wireOp",EDGE,"E51");Q3=makeQuery(id+"F0.imprint","IMPRINT",FACE,{"disambiguationData":[TD([[makeQuery(id+"F0.imprint","IMPRINT",EDGE,{"derivedFrom":subQ4}),-1.0]])]});}
            var Q4;
            Q4=makeQuery(id+"F0.imprint","IMPRINT",FACE,{"disambiguationData":[TD([[makeQuery(id+"F0.imprint","IMPRINT",EDGE,{"derivedFrom":sQuery(id+"F0.wireOp",EDGE,"E9.top")}),-1.0]])]});
            extrude(context, id + "F19", {"entities" : qUnion([Q0, Q1, Q2, Q3, Q4]), "operationType" : NewBodyOperationType.ADD, "oppositeDirection" : true, "depth" : 800 * mm, "offsetDistance" : 25 * mm});
        }
        {
            var Q0;
            Q0=makeQuery(id+"F19.opExtrude","CAP_FACE",FACE,{"disambiguationData":[OSD([sQuery(id+"F0.wireOp",EDGE,"E6"),sQuery(id+"F0.wireOp",EDGE,"E7"),sQuery(id+"F0.wireOp",EDGE,"E8"),sQuery(id+"F0.wireOp",EDGE,"E9.bottom"),sQuery(id+"F0.wireOp",EDGE,"E9.top"),sQuery(id+"F0.wireOp",EDGE,"E9.right"),sQuery(id+"F0.wireOp",EDGE,"E48"),sQuery(id+"F0.wireOp",EDGE,"E53")])],"isStart":false});
            var sketch = newSketch(context, id + "F20", { "sketchPlane" : qUnion([Q0])});
            skLineSegment(sketch, "E71.bottom", {"start": v(5200, -1400) * mm, "end": v(6600, -1400) * mm});
            skLineSegment(sketch, "E71.top", {"start": v(5200, -3000) * mm, "end": v(6600, -3000) * mm});
            skLineSegment(sketch, "E71.left", {"start": v(5200, -1400) * mm, "end": v(5200, -3000) * mm});
            skLineSegment(sketch, "E71.right", {"start": v(6600, -1400) * mm, "end": v(6600, -3000) * mm});
            skSolve(sketch);
        }
        {
            var Q0;
            Q0 = qSketchRegion(id + "F20", true);
            extrude(context, id + "F21", {"entities" : qUnion([Q0]), "operationType" : NewBodyOperationType.ADD, "depth" : 300 * mm, "offsetDistance" : 25 * mm});
        }
        {
            var Q0;
            Q0=qCreatedBy(makeId("Top.planeOp"),FACE);
            var sketch = newSketch(context, id + "F22", { "sketchPlane" : qUnion([Q0])});
            skLineSegment(sketch, "E72.0", {"start": v(0, 0) * mm, "end": v(0, 3000) * mm});
            skLineSegment(sketch, "E72.1", {"start": v(0, 3000) * mm, "end": v(5200, 3000) * mm});
            skLineSegment(sketch, "E72.2", {"start": v(6600, 3000) * mm, "end": v(5200, 3000) * mm});
            skLineSegment(sketch, "E72.3", {"start": v(6600, 1400) * mm, "end": v(6600, 3000) * mm});
            skLineSegment(sketch, "E72.4", {"start": v(5200, 1400) * mm, "end": v(3000, 1400) * mm});
            skLineSegment(sketch, "E72.5", {"start": v(5200, 1400) * mm, "end": v(6600, 1400) * mm});
            skLineSegment(sketch, "E72.6", {"start": v(3000, 1400) * mm, "end": v(3000, 0) * mm});
            skLineSegment(sketch, "E72.7", {"start": v(1600, 0) * mm, "end": v(3000, 0) * mm});
            skLineSegment(sketch, "E72.8", {"start": v(0, 0) * mm, "end": v(1600, 0) * mm});
            skLineSegment(sketch, "E73.bottom", {"start": v(-2600, 4000) * mm, "end": v(7100, 4000) * mm});
            skLineSegment(sketch, "E73.top", {"start": v(-2600, -2450) * mm, "end": v(7100, -2450) * mm});
            skLineSegment(sketch, "E73.left", {"start": v(-2600, 4000) * mm, "end": v(-2600, -2450) * mm});
            skLineSegment(sketch, "E73.right", {"start": v(7100, 4000) * mm, "end": v(7100, -2450) * mm});
            skSolve(sketch);
        }
        {
            var Q0;
            Q0 = qSketchRegion(id + "F22", true);
            extrude(context, id + "F23", {"entities" : qUnion([Q0]), "operationType" : NewBodyOperationType.ADD, "oppositeDirection" : true, "depth" : 200 * mm, "offsetDistance" : 25 * mm});
        }
    });
